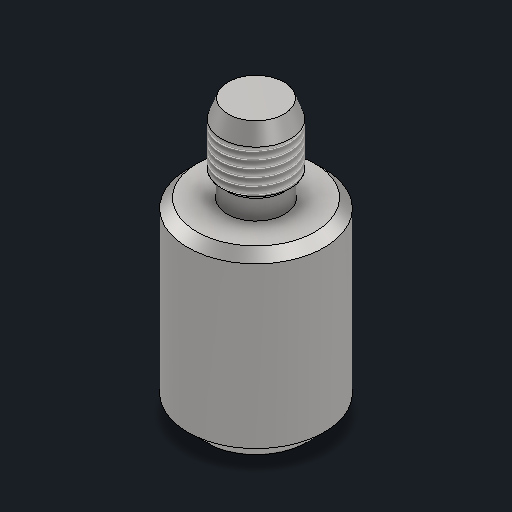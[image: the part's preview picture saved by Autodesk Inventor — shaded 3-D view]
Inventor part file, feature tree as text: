
AUTODESK INVENTOR PART (.ipt)
format: ipt  version: 2025.1 (Build 291241020, 241B)  size: 161,280 bytes
history: native  units: in
note: dims shown in document units (in); Inventor stores cm internally (conversion verified against a paired STEP export)
features: extrude x4, chamfer x4, sketch x3, thread x1, other x1
ambient origin geometry x8: Origin, YZ Plane, XZ Plane, XY Plane, X Axis, Y Axis, Z Axis, Center Point
bodies: Solid1 (feature_tree)
feature tree (13):
  sketch  "Sketch1"  dims[d0=0.375in d1=0.515in d2=0.0in]
  extrude  "Extrusion1"  Depth=0.515in TaperAngle=0.0deg
  extrude  "Extrusion2"  Depth=0.07in TaperAngle=0.0deg
  extrude  "Extrusion4"  Depth=0.1675in
  extrude  "Extrusion3"  Depth=0.1675in TaperAngle=0.0deg
  chamfer  "Chamfer2"  Distance=0.025in Angle=45.0deg
  chamfer  "Chamfer1"  Distance=0.1675in
  chamfer  "Chamfer3"  Distance=0.19in
  chamfer  "Chamfer4"  Distance=0.016in Angle=30.0deg
  thread  "Thread3"  [1 undecoded]
  sketch  "Sketch2"  dims[d3=0.1575in d4=0.07in d5=0.0in]
  sketch  "Sketch3"  dims[d6=0.05in d7=0.125in d8=45.0deg d9=0.05in d10=0.05in d11=0.0in d12=0.025in d13=0.125in d14=45.0deg d17=0.1675in d18=0.0in d19=0.19in d22=0.016in d23=0.125in d24=30.0deg d25=0.05in d26=0.125in d27=0.1374in d28=0.2375in d29=0.0in]
  other  "Finish1"
note: 1 required parameter value undecoded (feature->parameter linkage not recoverable at this tier; creation-order binding heuristic only, values carry confidence <= 0.55)
